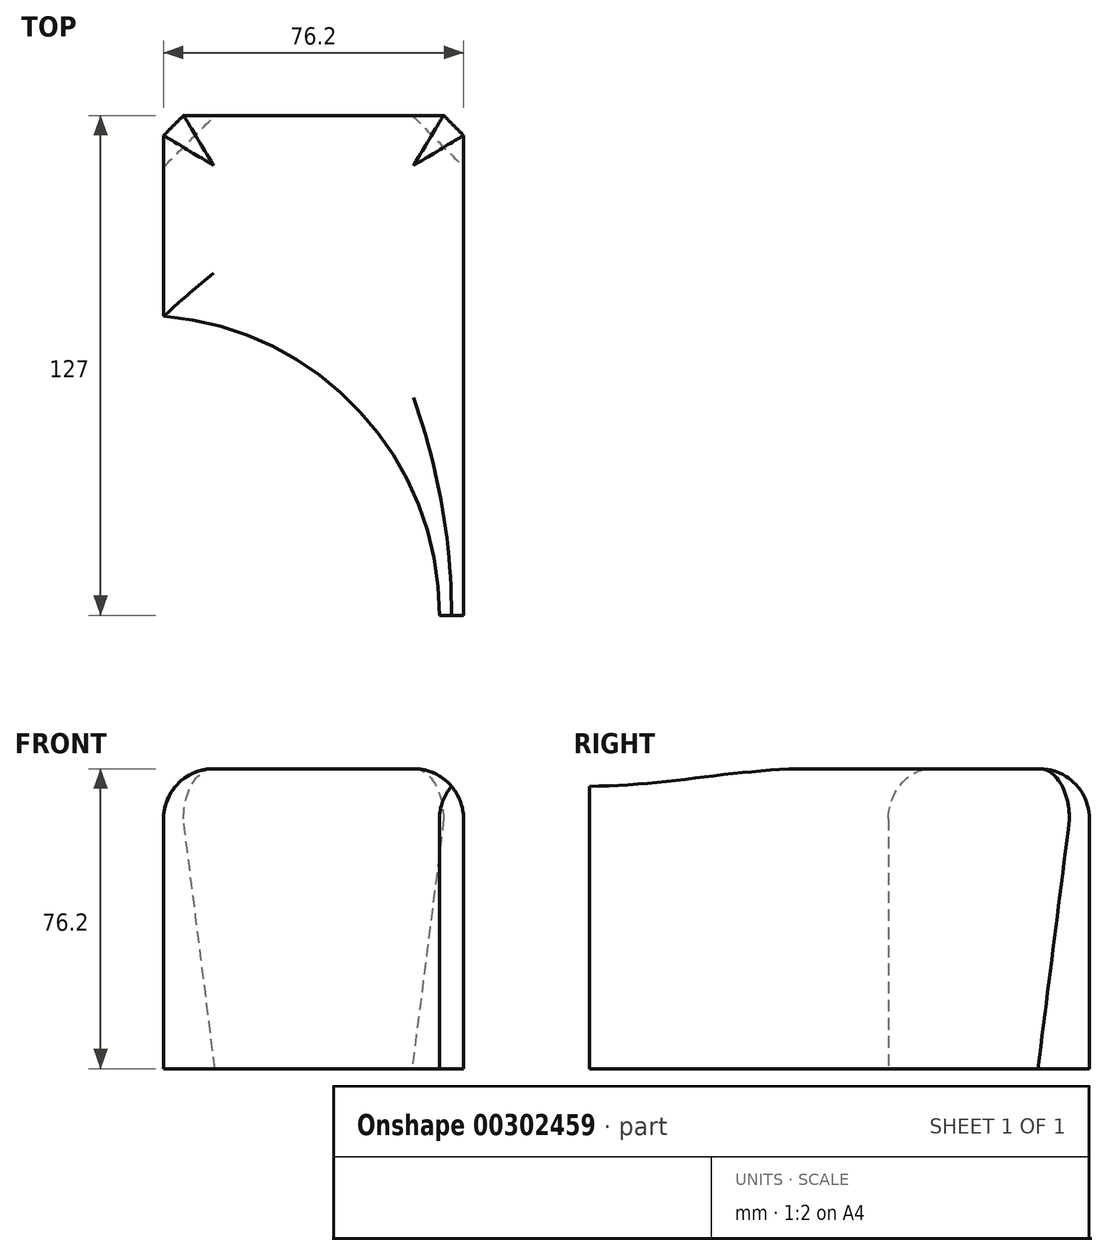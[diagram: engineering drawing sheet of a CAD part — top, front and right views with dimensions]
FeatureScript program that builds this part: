
annotation { "Feature Type Name" : "Feature", "Feature Type Description" : "" }
export const myFeature = defineFeature(function(context is Context, id is Id, definition is map)
    precondition{}
    {
        {
            var Q0;
            Q0=qCreatedBy(makeId("Top.planeOp"),FACE);
            var sketch = newSketch(context, id + "F0", { "sketchPlane" : qUnion([Q0])});
            skLineSegment(sketch, "E0", {"start": v(0, 0) * mm, "end": v(76.2, 0) * mm});
            skLineSegment(sketch, "E1", {"start": v(76.2, 0) * mm, "end": v(76.2, 127) * mm});
            skLineSegment(sketch, "E2", {"start": v(76.2, 127) * mm, "end": v(0, 127) * mm});
            skLineSegment(sketch, "E3", {"start": v(0, 127) * mm, "end": v(0, 0) * mm});
            skSolve(sketch);
        }
        {
            var Q0;
            Q0 = qSketchRegion(id + "F0", true);
            extrude(context, id + "F1", {"entities" : qUnion([Q0]), "depth" : 76.2 * mm});
        }
        {
            var Q0;
            Q0=qCreatedBy(makeId("Top.planeOp"),FACE);
            var sketch = newSketch(context, id + "F2", { "sketchPlane" : qUnion([Q0])});
            skPoint(sketch, "E4", {"position": v(-6.1, 0) * mm});
            skCircle(sketch, "E5", {"center": v(-6.1, 0) * mm, "radius": 76.2 * mm});
            skSolve(sketch);
        }
        {
            var Q0;
            Q0=makeQuery(id+"F2.imprint","IMPRINT",FACE,{"disambiguationData":[TD([[makeQuery(id+"F2.imprint","IMPRINT",EDGE,{"derivedFrom":sQuery(id+"F2.wireOp",EDGE,"E5")}),1.0]])]});
            extrude(context, id + "F3", {"entities" : qUnion([Q0]), "depth" : 76.2 * mm});
        }
        {
            var Q0;
            Q0=makeQuery(id+"F3.opExtrude","SWEPT_BODY",BODY,{"disambiguationData":[OSD([sQuery(id+"F2.wireOp",EDGE,"E5")])]});
            var Q1;
            Q1=makeQuery(id+"F1.opExtrude","SWEPT_BODY",BODY,{"disambiguationData":[OSD([sQuery(id+"F0.wireOp",EDGE,"E0"),sQuery(id+"F0.wireOp",EDGE,"E1"),sQuery(id+"F0.wireOp",EDGE,"E2"),sQuery(id+"F0.wireOp",EDGE,"E3")])]});
            booleanBodies(context, id + "F4", {"operationType" : BooleanOperationType.SUBTRACTION, "tools" : qUnion([Q0]), "targets" : qUnion([Q1])});
        }
        {
            var Q0;
            Q0=makeQuery(id+"F1.opExtrude","CAP_FACE",FACE,{"disambiguationData":[OSD([sQuery(id+"F0.wireOp",EDGE,"E0"),sQuery(id+"F0.wireOp",EDGE,"E1"),sQuery(id+"F0.wireOp",EDGE,"E2"),sQuery(id+"F0.wireOp",EDGE,"E3")])],"isStart":false});
            fillet(context, id + "F5", {"entities" : qUnion([Q0]), "radius" : 12.7 * mm, "tangentPropagation" : true, "allowEdgeOverflow" : false});
        }
        {
            var Q0;
            {var subQ0=sQuery(id+"F0.wireOp",EDGE,"E1");Q0=makeQuery(id+"F5.opFillet","BLEND_EDGE",EDGE,{"blendedFrom":[makeQuery(id+"F1.opExtrude","CAP_EDGE",EDGE,{"disambiguationData":[OSD([subQ0])],"isStart":false}),makeQuery(id+"F1.opExtrude","CAP_FACE",FACE,{"disambiguationData":[OSD([sQuery(id+"F0.wireOp",EDGE,"E0"),subQ0,sQuery(id+"F0.wireOp",EDGE,"E2"),sQuery(id+"F0.wireOp",EDGE,"E3")])],"isStart":false})],"blendedInto":[makeQuery(id+"F1.opExtrude","CAP_FACE",FACE,{"disambiguationData":[OSD([sQuery(id+"F0.wireOp",EDGE,"E0"),subQ0,sQuery(id+"F0.wireOp",EDGE,"E2"),sQuery(id+"F0.wireOp",EDGE,"E3")])],"isStart":false})]});}
            var Q1;
            {var subQ0=sQuery(id+"F0.wireOp",EDGE,"E2");Q1=makeQuery(id+"F5.opFillet","BLEND_EDGE",EDGE,{"blendedFrom":[makeQuery(id+"F1.opExtrude","CAP_EDGE",EDGE,{"disambiguationData":[OSD([subQ0])],"isStart":false}),makeQuery(id+"F1.opExtrude","CAP_FACE",FACE,{"disambiguationData":[OSD([sQuery(id+"F0.wireOp",EDGE,"E0"),sQuery(id+"F0.wireOp",EDGE,"E1"),subQ0,sQuery(id+"F0.wireOp",EDGE,"E3")])],"isStart":false})],"blendedInto":[makeQuery(id+"F1.opExtrude","CAP_FACE",FACE,{"disambiguationData":[OSD([sQuery(id+"F0.wireOp",EDGE,"E0"),sQuery(id+"F0.wireOp",EDGE,"E1"),subQ0,sQuery(id+"F0.wireOp",EDGE,"E3")])],"isStart":false})]});}
            var Q2;
            {var subQ0=sQuery(id+"F0.wireOp",EDGE,"E3");Q2=makeQuery(id+"F5.opFillet","BLEND_EDGE",EDGE,{"blendedFrom":[makeQuery(id+"F1.opExtrude","CAP_EDGE",EDGE,{"disambiguationData":[OSD([subQ0])],"isStart":false}),makeQuery(id+"F1.opExtrude","CAP_FACE",FACE,{"disambiguationData":[OSD([sQuery(id+"F0.wireOp",EDGE,"E0"),sQuery(id+"F0.wireOp",EDGE,"E1"),sQuery(id+"F0.wireOp",EDGE,"E2"),subQ0])],"isStart":false})],"blendedInto":[makeQuery(id+"F1.opExtrude","CAP_FACE",FACE,{"disambiguationData":[OSD([sQuery(id+"F0.wireOp",EDGE,"E0"),sQuery(id+"F0.wireOp",EDGE,"E1"),sQuery(id+"F0.wireOp",EDGE,"E2"),subQ0])],"isStart":false})]});}
            var Q3;
            Q3=makeQuery(id+"F5.opFillet","BLEND_EDGE",EDGE,{"blendedFrom":[makeQuery(id+"F1.opExtrude","CAP_EDGE",EDGE,{"disambiguationData":[OSD([sQuery(id+"F0.wireOp",EDGE,"E2")])],"isStart":false}),makeQuery(id+"F1.opExtrude","CAP_EDGE",EDGE,{"disambiguationData":[OSD([sQuery(id+"F0.wireOp",EDGE,"E3")])],"isStart":false})],"blendedInto":[]});
            var Q4;
            Q4=makeQuery(id+"F5.opFillet","BLEND_EDGE",EDGE,{"blendedFrom":[makeQuery(id+"F4.opBoolean","COPY",EDGE,{"derivedFrom":makeQuery(id+"F3.opExtrude","CAP_EDGE",EDGE,{"disambiguationData":[OSD([sQuery(id+"F2.wireOp",EDGE,"E5")])],"isStart":false})}),makeQuery(id+"F1.opExtrude","CAP_FACE",FACE,{"disambiguationData":[OSD([sQuery(id+"F0.wireOp",EDGE,"E0"),sQuery(id+"F0.wireOp",EDGE,"E1"),sQuery(id+"F0.wireOp",EDGE,"E2"),sQuery(id+"F0.wireOp",EDGE,"E3")])],"isStart":false})],"blendedInto":[makeQuery(id+"F1.opExtrude","CAP_FACE",FACE,{"disambiguationData":[OSD([sQuery(id+"F0.wireOp",EDGE,"E0"),sQuery(id+"F0.wireOp",EDGE,"E1"),sQuery(id+"F0.wireOp",EDGE,"E2"),sQuery(id+"F0.wireOp",EDGE,"E3")])],"isStart":false})]});
            var Q5;
            Q5=makeQuery(id+"F5.opFillet","BLEND_EDGE",EDGE,{"blendedFrom":[makeQuery(id+"F1.opExtrude","CAP_EDGE",EDGE,{"disambiguationData":[OSD([sQuery(id+"F0.wireOp",EDGE,"E1")])],"isStart":false}),makeQuery(id+"F4.opBoolean","COPY",EDGE,{"derivedFrom":makeQuery(id+"F3.opExtrude","CAP_EDGE",EDGE,{"disambiguationData":[OSD([sQuery(id+"F2.wireOp",EDGE,"E5")])],"isStart":false})})],"blendedInto":[]});
            var Q6;
            {var subQ0=sQuery(id+"F0.wireOp",EDGE,"E1");Q6=makeQuery(id+"F5.opFillet","BLEND_EDGE",EDGE,{"blendedFrom":[makeQuery(id+"F1.opExtrude","CAP_EDGE",EDGE,{"disambiguationData":[OSD([subQ0])],"isStart":false}),makeQuery(id+"F1.opExtrude","SWEPT_FACE",FACE,{"disambiguationData":[OSD([subQ0])]})],"blendedInto":[makeQuery(id+"F1.opExtrude","SWEPT_FACE",FACE,{"disambiguationData":[OSD([subQ0])]})]});}
            var Q7;
            Q7=makeQuery(id+"F5.opFillet","BLEND_EDGE",EDGE,{"blendedFrom":[makeQuery(id+"F1.opExtrude","CAP_EDGE",EDGE,{"disambiguationData":[OSD([sQuery(id+"F0.wireOp",EDGE,"E1")])],"isStart":false}),makeQuery(id+"F1.opExtrude","CAP_EDGE",EDGE,{"disambiguationData":[OSD([sQuery(id+"F0.wireOp",EDGE,"E2")])],"isStart":false})],"blendedInto":[]});
            var Q8;
            {var subQ0=sQuery(id+"F0.wireOp",EDGE,"E2");Q8=makeQuery(id+"F5.opFillet","BLEND_EDGE",EDGE,{"blendedFrom":[makeQuery(id+"F1.opExtrude","CAP_EDGE",EDGE,{"disambiguationData":[OSD([subQ0])],"isStart":false}),makeQuery(id+"F1.opExtrude","SWEPT_FACE",FACE,{"disambiguationData":[OSD([subQ0])]})],"blendedInto":[makeQuery(id+"F1.opExtrude","SWEPT_FACE",FACE,{"disambiguationData":[OSD([subQ0])]})]});}
            var Q9;
            {var subQ0=sQuery(id+"F0.wireOp",EDGE,"E3");Q9=makeQuery(id+"F5.opFillet","BLEND_EDGE",EDGE,{"blendedFrom":[makeQuery(id+"F1.opExtrude","CAP_EDGE",EDGE,{"disambiguationData":[OSD([subQ0])],"isStart":false}),makeQuery(id+"F1.opExtrude","SWEPT_FACE",FACE,{"disambiguationData":[OSD([subQ0])]})],"blendedInto":[makeQuery(id+"F1.opExtrude","SWEPT_FACE",FACE,{"disambiguationData":[OSD([subQ0])]})]});}
            var Q10;
            Q10=makeQuery(id+"F5.opFillet","BLEND_EDGE",EDGE,{"blendedFrom":[makeQuery(id+"F4.opBoolean","COPY",EDGE,{"derivedFrom":makeQuery(id+"F3.opExtrude","CAP_EDGE",EDGE,{"disambiguationData":[OSD([sQuery(id+"F2.wireOp",EDGE,"E5")])],"isStart":false})}),makeQuery(id+"F1.opExtrude","CAP_EDGE",EDGE,{"disambiguationData":[OSD([sQuery(id+"F0.wireOp",EDGE,"E3")])],"isStart":false})],"blendedInto":[]});
            var Q11;
            {var subQ0=sQuery(id+"F2.wireOp",EDGE,"E5");Q11=makeQuery(id+"F5.opFillet","BLEND_EDGE",EDGE,{"blendedFrom":[makeQuery(id+"F4.opBoolean","COPY",EDGE,{"derivedFrom":makeQuery(id+"F3.opExtrude","CAP_EDGE",EDGE,{"disambiguationData":[OSD([subQ0])],"isStart":false})}),makeQuery(id+"F4.opBoolean","COPY",FACE,{"derivedFrom":makeQuery(id+"F3.opExtrude","SWEPT_FACE",FACE,{"disambiguationData":[OSD([subQ0])]})})],"blendedInto":[makeQuery(id+"F4.opBoolean","COPY",FACE,{"derivedFrom":makeQuery(id+"F3.opExtrude","SWEPT_FACE",FACE,{"disambiguationData":[OSD([subQ0])]})})]});}
            chamfer(context, id + "F6", {"entities" : qUnion([Q0, Q1, Q2, Q3, Q4, Q5, Q6, Q7, Q8, Q9, Q10, Q11]), "width" : 5.08 * mm, "tangentPropagation" : true});
        }
    });
